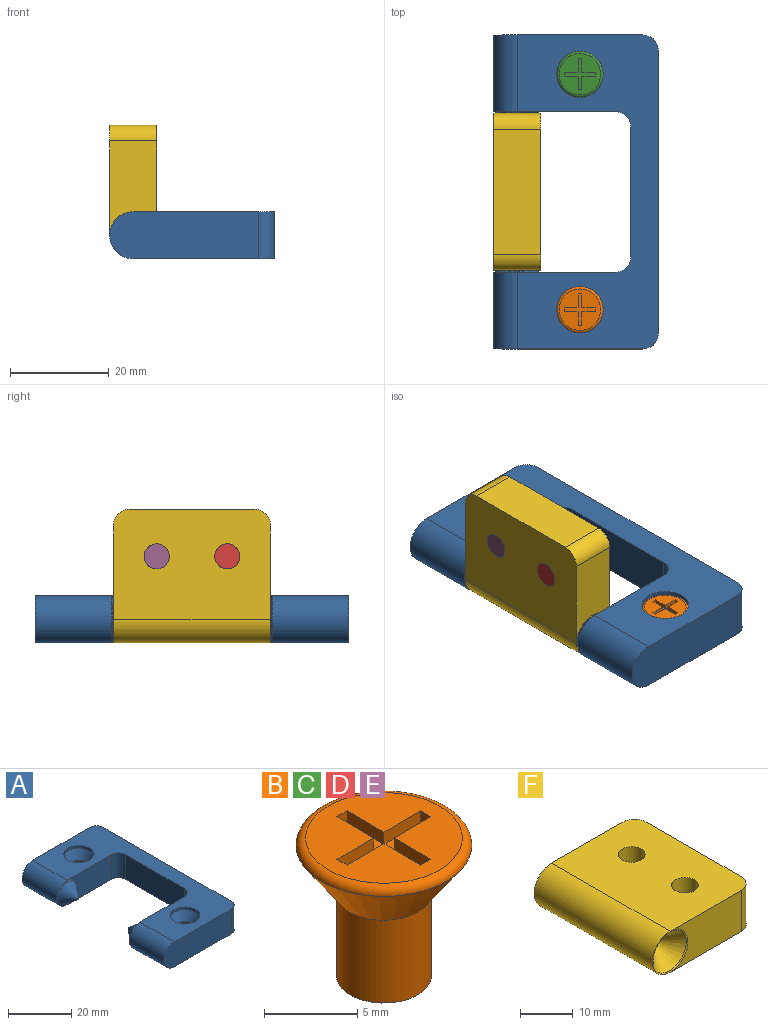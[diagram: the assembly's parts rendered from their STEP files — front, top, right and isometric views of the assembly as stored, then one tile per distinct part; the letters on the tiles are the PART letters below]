
ASSEMBLY  parts=6 mates=5
PART A: 26 faces, bbox 34.3x63.5x11.5 mm
  f0: plane 19.84x9.53mm, normal (0,-1,0), area 153.4mm2, adj f4,f6,f19,f23
  f1: plane 19.84x9.53mm, normal (0,1,0), area 153.4mm2, adj f4,f6,f18,f22
  f2: cylinder r=4.76mm len=15.48mm, axis (0,1,0), area 231.6mm2, adj f4,f6,f8,f19
  f3: cylinder r=4.76mm len=15.48mm, axis (0,1,0), area 231.6mm2, adj f4,f6,f7,f18
  f4: plane 63.5x28.58mm, normal (0,0,-1), area 1024.9mm2, adj f0,f1,f2,f3,f5,f7,f8,f9
  f5: plane 57.15x9.53mm, normal (1,0,0), area 544.4mm2, adj f4,f6,f24,f25
  f6: plane 63.5x28.58mm, normal (0,0,1), area 926.7mm2, adj f0,f1,f2,f3,f5,f7,f8,f9
  f7: plane 30.16x9.53mm, normal (0,-1,0), area 277.6mm2, adj f3,f4,f6,f25
  f8: plane 30.16x9.53mm, normal (0,1,0), area 277.6mm2, adj f2,f4,f6,f24
  f9: plane 26.19x9.53mm, normal (-1,0,0), area 249.5mm2, adj f4,f6,f22,f23
  f10: cylinder r=2.54mm len=5.43mm, axis (0,0,1), area 86.6mm2, adj f4,f11
  f11: cone r=4.7mm half-angle=35deg, axis (0,0,1), area 85.6mm2, adj f10,f12
  f12: cylinder r=4.7mm len=9.4mm, axis (0,0,1), area 30mm2, adj f6,f11
  f13: cylinder r=2.54mm len=5.43mm, axis (0,0,1), area 86.6mm2, adj f4,f14
  f14: cone r=4.7mm half-angle=35deg, axis (0,0,1), area 85.6mm2, adj f13,f15
  f15: cylinder r=4.7mm len=9.4mm, axis (0,0,1), area 30mm2, adj f6,f14
  f16: sphere r=0.4mm, area 0.4mm2, adj f17
  f17: cone r=4.15mm half-angle=40deg, axis (0,-1,0), area 83.9mm2, adj f16,f18
  f18: torus R=4.76mm, axis (0,1,0), area 19.3mm2, adj f1,f3,f17
  f19: torus R=4.76mm, axis (0,1,0), area 19.3mm2, adj f0,f2,f20
  f20: cone r=4.15mm half-angle=40deg, axis (0,1,0), area 83.9mm2, adj f19,f21
  f21: sphere r=0.4mm, area 0.4mm2, adj f20
  f22: cylinder r=3.17mm len=9.53mm, axis (0,0,-1), area 47.5mm2, adj f1,f4,f6,f9
  f23: cylinder r=3.17mm len=9.53mm, axis (0,0,1), area 47.5mm2, adj f0,f4,f6,f9
  f24: cylinder r=3.17mm len=9.53mm, axis (0,0,1), area 47.5mm2, adj f4,f5,f6,f8
  f25: cylinder r=3.17mm len=9.53mm, axis (0,0,-1), area 47.5mm2, adj f4,f5,f6,f7
PART B: 18 faces, bbox 10.2x10.2x9 mm
  f0: plane 8.38x8.38mm, normal (0,0,1), area 46.1mm2, adj f4,f5,f6,f7,f8,f9,f10,f11
  f1: plane 5.08x5.08mm, normal (0,0,-1), area 20.3mm2, adj f2
  f2: cylinder r=2.54mm len=5.43mm, axis (0,0,-1), area 86.6mm2, adj f1,f3
  f3: cone r=4.7mm half-angle=35deg, axis (0,0,1), area 85.6mm2, adj f2,f4
  f4: torus R=4.19mm, axis (0,0,-1), area 22.6mm2, adj f0,f3
  f5: plane 0.79x0.76mm, normal (0,1,0), area 0.6mm2, adj f0,f6,f16,f17
  f6: plane 2.79x0.79mm, normal (-1,0,0), area 2.2mm2, adj f0,f5,f7,f17
  f7: plane 2.79x0.79mm, normal (0,1,0), area 2.2mm2, adj f0,f6,f8,f17
  f8: plane 0.79x0.76mm, normal (-1,0,0), area 0.6mm2, adj f0,f7,f9,f17
  f9: plane 2.79x0.79mm, normal (0,-1,0), area 2.2mm2, adj f0,f8,f10,f17
  f10: plane 2.79x0.79mm, normal (-1,0,0), area 2.2mm2, adj f0,f9,f11,f17
  f11: plane 0.79x0.76mm, normal (0,-1,0), area 0.6mm2, adj f0,f10,f12,f17
  f12: plane 2.79x0.79mm, normal (1,0,0), area 2.2mm2, adj f0,f11,f13,f17
  f13: plane 2.79x0.79mm, normal (0,-1,0), area 2.2mm2, adj f0,f12,f14,f17
  f14: plane 0.79x0.76mm, normal (1,0,0), area 0.6mm2, adj f0,f13,f15,f17
  f15: plane 2.79x0.79mm, normal (0,1,0), area 2.2mm2, adj f0,f14,f16,f17
  f16: plane 2.79x0.79mm, normal (1,0,0), area 2.2mm2, adj f0,f5,f15,f17
  f17: plane 6.35x6.35mm, normal (0,0,1), area 9.1mm2, adj f5,f6,f7,f8,f9,f10,f11,f12
PART C: same geometry as B
PART D: same geometry as B
PART E: same geometry as B
PART F: 20 faces, bbox 27.7x31.8x10.9 mm
  f0: plane 25.4x9.53mm, normal (1,0,0), area 241.9mm2, adj f1,f3,f18,f19
  f1: plane 31.75x22.23mm, normal (0,0,1), area 660.8mm2, adj f0,f2,f4,f5,f8,f11,f18,f19
  f2: cylinder r=4.76mm len=31.75mm, axis (0,1,0), area 475mm2, adj f1,f3,f12,f17
  f3: plane 31.75x22.23mm, normal (0,0,-1), area 562.6mm2, adj f0,f2,f4,f5,f6,f9,f18,f19
  f4: plane 19.05x9.53mm, normal (0,-1,0), area 145.8mm2, adj f1,f3,f17,f19
  f5: plane 19.05x9.53mm, normal (0,1,0), area 145.8mm2, adj f1,f3,f12,f18
  f6: cylinder r=4.7mm len=9.4mm, axis (0,0,-1), area 30mm2, adj f3,f7
  f7: cone r=2.54mm half-angle=35deg, axis (0,0,-1), area 85.6mm2, adj f6,f8
  f8: cylinder r=2.54mm len=5.43mm, axis (0,0,-1), area 86.6mm2, adj f1,f7
  f9: cylinder r=4.7mm len=9.4mm, axis (0,0,-1), area 30mm2, adj f3,f10
  f10: cone r=2.54mm half-angle=35deg, axis (0,0,-1), area 85.6mm2, adj f9,f11
  f11: cylinder r=2.54mm len=5.43mm, axis (0,0,-1), area 86.6mm2, adj f1,f10
  f12: torus R=4.76mm, axis (0,-1,0), area 10mm2, adj f2,f5,f13
  f13: cone r=4.46mm half-angle=40deg, axis (0,1,0), area 95.3mm2, adj f12,f14
  f14: sphere r=0.79mm, area 1.4mm2, adj f13
  f15: sphere r=0.79mm, area 1.4mm2, adj f16
  f16: cone r=4.46mm half-angle=40deg, axis (0,-1,0), area 95.3mm2, adj f15,f17
  f17: torus R=4.76mm, axis (0,-1,0), area 10mm2, adj f2,f4,f16
  f18: cylinder r=3.17mm len=9.53mm, axis (0,0,1), area 47.5mm2, adj f0,f1,f3,f5
  f19: cylinder r=3.17mm len=9.53mm, axis (0,0,-1), area 47.5mm2, adj f0,f1,f3,f4
PLACE A t=(-16.36,0,4.76)mm
PLACE B t=(-21.44,-23.81,0)mm
PLACE C t=(-21.44,23.81,0)mm
PLACE D rot(axis=(0,1,0),90deg) t=(-21.12,-7.14,35.24)mm
PLACE E rot(axis=(0,1,0),90deg) t=(-21.12,7.14,35.24)mm
PLACE F rot(axis=(0,-1,0),90deg) t=(-16.36,0,4.76)mm
MATE fastened F.f7 <-> D.f2  axis (-1,0,0) through (-21.12,-7.14,17.46)mm
MATE fastened A.f14 <-> C.f2  axis (0,0,-1) through (-3.66,23.81,0)mm
MATE revolute A.f2 <-> F.f2  axis (0,-1,0) through (-16.36,16.27,4.76)mm
MATE fastened F.f10 <-> E.f2  axis (-1,0,0) through (-21.12,7.14,17.46)mm
MATE fastened A.f10 <-> B.f2  axis (0,0,-1) through (-3.66,-23.81,0)mm
